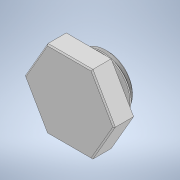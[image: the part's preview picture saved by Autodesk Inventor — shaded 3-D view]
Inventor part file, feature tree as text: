
AUTODESK INVENTOR PART (.ipt)
format: ipt  version: 2021 (Build 250183000, 183)  size: 224,768 bytes
history: native  units: mm
features: sketch x7, extrude x5, helix x1, revolve x1, chamfer x1, projected_geometry x1
ambient origin geometry x8: Origin, YZ Plane, XZ Plane, XY Plane, X Axis, Y Axis, Z Axis, Center Point
bodies: Solid1 (feature_tree)
feature tree (16):
  extrude  "Extrusion1"  Depth=8.0mm TaperAngle=0.0deg
  extrude  "Extrusion2"  Depth=8.0mm TaperAngle=0.0deg
  helix  "Coil1"  [1 undecoded]
  extrude  "Extrusion3"  Depth=23.5mm
  revolve  "Revolution1"  Angle=60.0deg
  chamfer  "Chamfer1"  Distance=8.0mm
  extrude  "Extrusion4"  Depth=10.0mm
  extrude  "Extrusion5"  TaperAngle=45.0deg  [1 undecoded]
  sketch  "Sketch1"  dims[d0=32.0mm d1=8.0mm d2=0.0mm]
  sketch  "Sketch2"  dims[d3=19.85mm d4=8.0mm d5=0.0mm d6=19.85mm]
  sketch  "Sketch3"  dims[d7=21.8mm d8=23.5mm]
  sketch  "Sketch4"  dims[d9=30.0deg d10=60.0deg]
  sketch  "Sketch5"  dims[d11=1.5mm]
  sketch  "Sketch6"  dims[d12=3.0mm d13=15.0mm d14=10.0mm d15=0.0mm d16=90.0deg d17=90.0deg d18=0.0mm d19=0.0mm d20=8.0mm d21=0.0mm]
  sketch  "Sketch7"  dims[d22=10.0mm d23=11.8mm d24=45.0deg d25=90.0deg d26=18.0mm d27=35.0mm d28=0.0mm d29=1.5mm d30=0.0mm d31=0.0mm d32=0.5mm d33=2.0mm d34=45.0deg]
  projected_geometry  "Projected Loop1"
note: 2 required parameter values undecoded (feature->parameter linkage not recoverable at this tier; creation-order binding heuristic only, values carry confidence <= 0.55)
